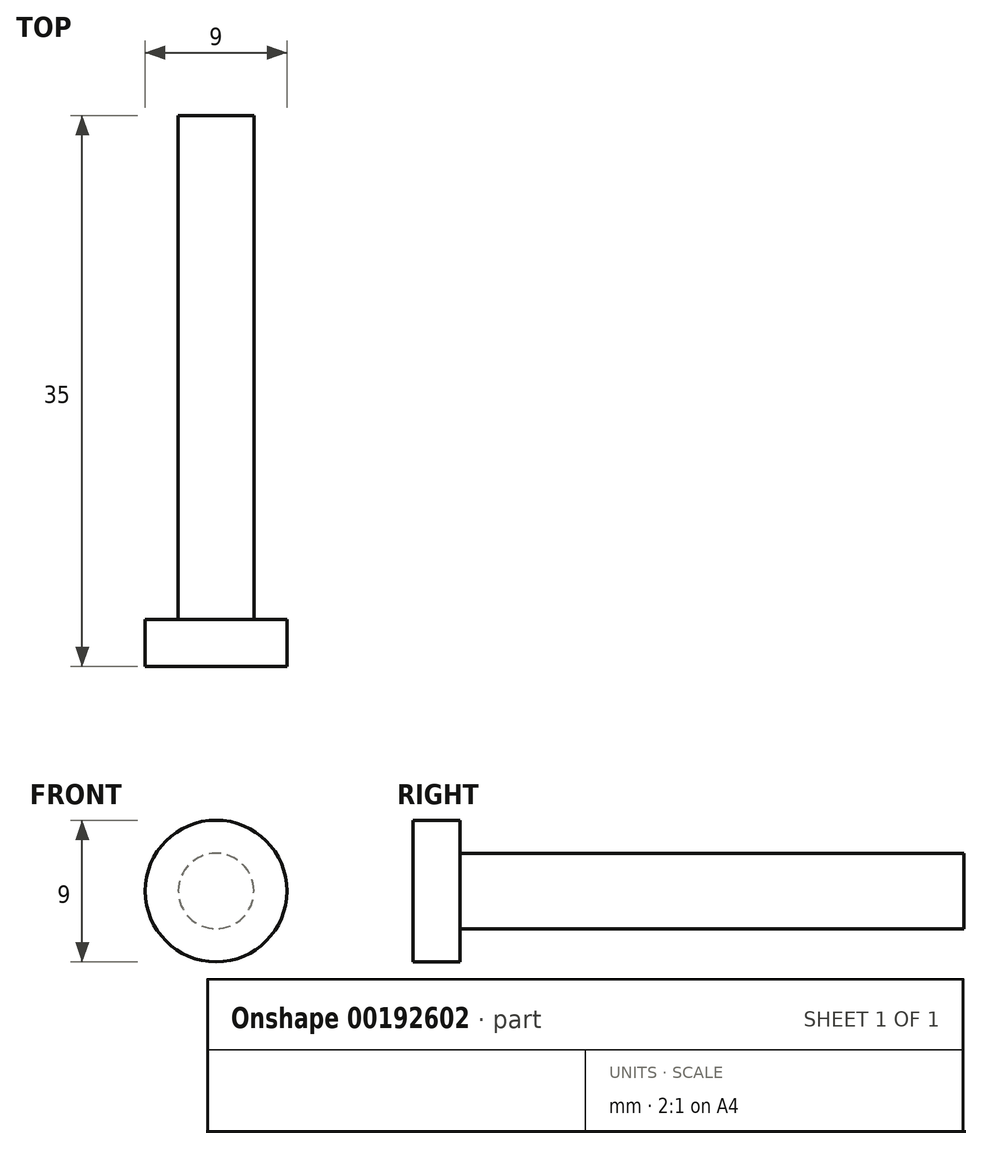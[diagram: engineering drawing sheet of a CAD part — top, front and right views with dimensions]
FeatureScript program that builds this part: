
annotation { "Feature Type Name" : "Feature", "Feature Type Description" : "" }
export const myFeature = defineFeature(function(context is Context, id is Id, definition is map)
    precondition{}
    {
        {
            var Q0;
            Q0=qCreatedBy(makeId("Front.planeOp"),FACE);
            var sketch = newSketch(context, id + "F0", { "sketchPlane" : qUnion([Q0])});
            skCircle(sketch, "E0", {"center": v(0, 0) * mm, "radius": 2.4 * mm});
            skSolve(sketch);
        }
        {
            var Q0;
            Q0=makeQuery(id+"F0.imprint","IMPRINT",FACE,{"disambiguationData":[TD([[makeQuery(id+"F0.imprint","IMPRINT",EDGE,{"derivedFrom":sQuery(id+"F0.wireOp",EDGE,"E0")}),1.0]])]});
            extrude(context, id + "F1", {"entities" : qUnion([Q0]), "depth" : 32 * mm});
        }
        {
            var Q0;
            Q0=makeQuery(id+"F1.opExtrude","CAP_FACE",FACE,{"disambiguationData":[OSD([sQuery(id+"F0.wireOp",EDGE,"E0")])],"isStart":false});
            var sketch = newSketch(context, id + "F2", { "sketchPlane" : qUnion([Q0])});
            skCircle(sketch, "E1", {"center": v(0, 0) * mm, "radius": 4.5 * mm});
            skSolve(sketch);
        }
        {
            var Q0;
            Q0=makeQuery(id+"F2.imprint","IMPRINT",FACE,{"disambiguationData":[TD([[makeQuery(id+"F2.imprint","IMPRINT",EDGE,{"derivedFrom":sQuery(id+"F2.wireOp",EDGE,"E1")}),1.0]])]});
            var Q1;
            Q1=makeQuery(id+"F2.imprint","IMPRINT",FACE,{"disambiguationData":[TD([[makeQuery(id+"F2.imprint","IMPRINT",EDGE,{"derivedFrom":makeQuery(id+"F1.opExtrude","CAP_EDGE",EDGE,{"disambiguationData":[OSD([sQuery(id+"F0.wireOp",EDGE,"E0")])],"isStart":false})}),1.0]])]});
            extrude(context, id + "F3", {"entities" : qUnion([Q0, Q1]), "operationType" : NewBodyOperationType.ADD, "depth" : 3 * mm});
        }
    });
